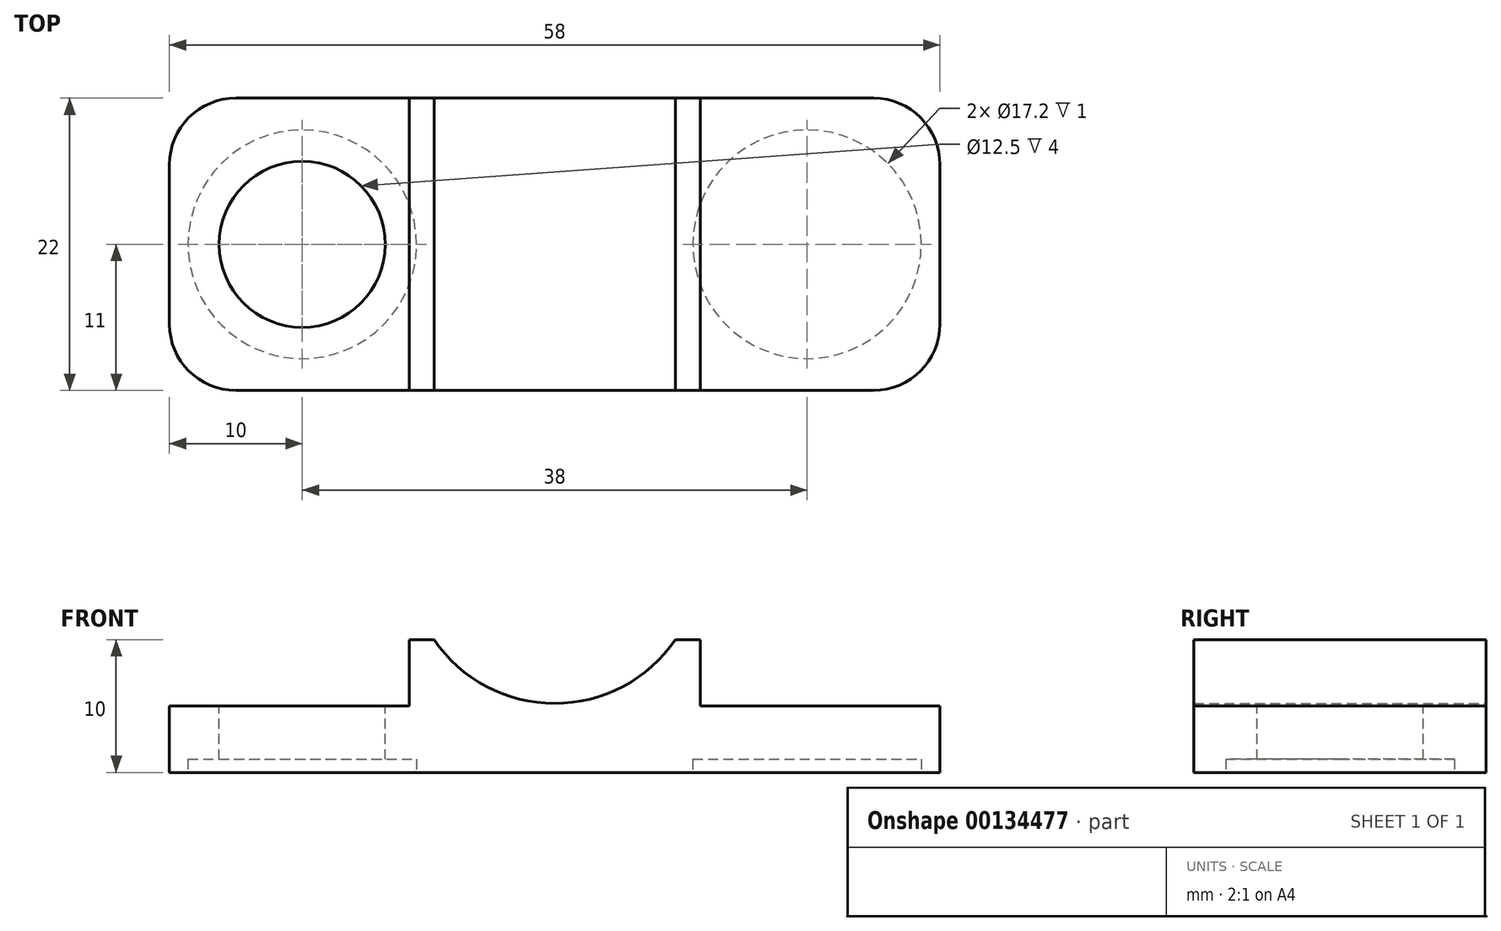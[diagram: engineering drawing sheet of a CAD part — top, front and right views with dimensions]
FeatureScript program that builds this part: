
annotation { "Feature Type Name" : "Feature", "Feature Type Description" : "" }
export const myFeature = defineFeature(function(context is Context, id is Id, definition is map)
    precondition{}
    {
        {
            var Q0;
            Q0=qCreatedBy(makeId("Top.planeOp"),FACE);
            var sketch = newSketch(context, id + "F0", { "sketchPlane" : qUnion([Q0])});
            skLineSegment(sketch, "E0.bottom", {"start": v(11, -17.54) * mm, "end": v(-11, -17.54) * mm});
            skLineSegment(sketch, "E0.top", {"start": v(11, 17.54) * mm, "end": v(-11, 17.54) * mm});
            skLineSegment(sketch, "E0.left", {"start": v(11, -17.54) * mm, "end": v(11, 17.54) * mm});
            skLineSegment(sketch, "E0.right", {"start": v(-11, -17.54) * mm, "end": v(-11, 17.54) * mm});
            skPoint(sketch, "E0.middle", {"position": v(0, 0) * mm});
            skCircle(sketch, "E1.cCircle", {"center": v(-19, 0) * mm, "radius": 7.5 * mm, "construction": true});
            skLineSegment(sketch, "E1.0", {"start": v(-14.67, -7.5) * mm, "end": v(-23.33, -7.5) * mm});
            skLineSegment(sketch, "E1.1", {"start": v(-23.33, -7.5) * mm, "end": v(-27.66, 0) * mm});
            skLineSegment(sketch, "E1.2", {"start": v(-27.66, 0) * mm, "end": v(-23.33, 7.5) * mm});
            skLineSegment(sketch, "E1.3", {"start": v(-23.33, 7.5) * mm, "end": v(-14.67, 7.5) * mm});
            skLineSegment(sketch, "E1.4", {"start": v(-14.67, 7.5) * mm, "end": v(-10.34, 0) * mm});
            skLineSegment(sketch, "E1.5", {"start": v(-10.34, 0) * mm, "end": v(-14.67, -7.5) * mm});
            skPoint(sketch, "E1.0.midPoint", {"position": v(-19, -7.5) * mm});
            skSolve(sketch);
        }
        {
            var Q0;
            Q0=qCreatedBy(makeId("Front.planeOp"),FACE);
            var sketch = newSketch(context, id + "F1", { "sketchPlane" : qUnion([Q0])});
            skArc(sketch, "E2", {"start": v(-9.09, 5) * mm, "mid": v(0, 0.2) * mm, "end": v(9.09, 5) * mm});
            skLineSegment(sketch, "E3", {"start": v(-10.95, 5) * mm, "end": v(-10.95, 0) * mm});
            skLineSegment(sketch, "E4", {"start": v(-10.95, 0) * mm, "end": v(-29, 0) * mm});
            skLineSegment(sketch, "E5", {"start": v(10.95, 5) * mm, "end": v(10.95, 0) * mm});
            skLineSegment(sketch, "E6", {"start": v(10.95, 0) * mm, "end": v(29, 0) * mm});
            skLineSegment(sketch, "E7", {"start": v(-19, 8.5) * mm, "end": v(-19, -9.59) * mm, "construction": true});
            skLineSegment(sketch, "E8", {"start": v(-29, -5) * mm, "end": v(-29, 0) * mm});
            skLineSegment(sketch, "E9", {"start": v(29, -5) * mm, "end": v(29, 0) * mm});
            skLineSegment(sketch, "E10", {"start": v(-29, -5) * mm, "end": v(29, -5) * mm});
            skLineSegment(sketch, "E11", {"start": v(10.95, 5) * mm, "end": v(9.09, 5) * mm});
            skLineSegment(sketch, "E12.trimOffspring", {"start": v(-9.09, 5) * mm, "end": v(-10.95, 5) * mm});
            skSolve(sketch);
        }
        {
            var Q0;
            Q0=qSketchRegion(id+"F1",true);
            extrude(context, id + "F2", {"entities" : qUnion([Q0]), "depth" : 22 * mm, "symmetric" : true});
        }
        {
            var Q0;
            Q0=qCreatedBy(makeId("Top.planeOp"),FACE);
            var sketch = newSketch(context, id + "F3", { "sketchPlane" : qUnion([Q0])});
            skCircle(sketch, "E13.0", {"center": v(-19, 0) * mm, "radius": 7.5 * mm, "construction": true});
            skCircle(sketch, "E14", {"center": v(-19, 0) * mm, "radius": 6.25 * mm});
            skSolve(sketch);
        }
        {
            var Q0;
            Q0=qSketchRegion(id+"F3",true);
            extrude(context, id + "F4", {"entities" : qUnion([Q0]), "operationType" : NewBodyOperationType.REMOVE, "endBound" : BoundingType.THROUGH_ALL, "oppositeDirection" : true, "depth" : 25 * mm});
        }
        {
            var Q0;
            Q0=makeQuery(id+"F2.opExtrude","CAP_EDGE",EDGE,{"disambiguationData":[OSD([sQuery(id+"F1.wireOp",EDGE,"E8")])],"isStart":false});
            var Q1;
            Q1=makeQuery(id+"F2.opExtrude","CAP_EDGE",EDGE,{"disambiguationData":[OSD([sQuery(id+"F1.wireOp",EDGE,"E8")])],"isStart":true});
            var Q2;
            Q2=makeQuery(id+"F2.opExtrude","CAP_EDGE",EDGE,{"disambiguationData":[OSD([sQuery(id+"F1.wireOp",EDGE,"E9")])],"isStart":false});
            var Q3;
            Q3=makeQuery(id+"F2.opExtrude","CAP_EDGE",EDGE,{"disambiguationData":[OSD([sQuery(id+"F1.wireOp",EDGE,"E9")])],"isStart":true});
            fillet(context, id + "F5", {"entities" : qUnion([Q0, Q1, Q2, Q3]), "radius" : 5 * mm, "tangentPropagation" : true, "allowEdgeOverflow" : false});
        }
        {
            var Q0;
            Q0=makeQuery(id+"F2.opExtrude","SWEPT_FACE",FACE,{"disambiguationData":[OSD([sQuery(id+"F1.wireOp",EDGE,"E10")])]});
            var sketch = newSketch(context, id + "F6", { "sketchPlane" : qUnion([Q0])});
            skCircle(sketch, "E15", {"center": v(-19, 0) * mm, "radius": 8.6 * mm});
            skCircle(sketch, "E16", {"center": v(19, 0) * mm, "radius": 8.6 * mm});
            skSolve(sketch);
        }
        {
            var Q0;
            Q0 = qSketchRegion(id + "F6", true);
            extrude(context, id + "F7", {"entities" : qUnion([Q0]), "operationType" : NewBodyOperationType.REMOVE, "oppositeDirection" : true, "depth" : 1 * mm});
        }
    });
